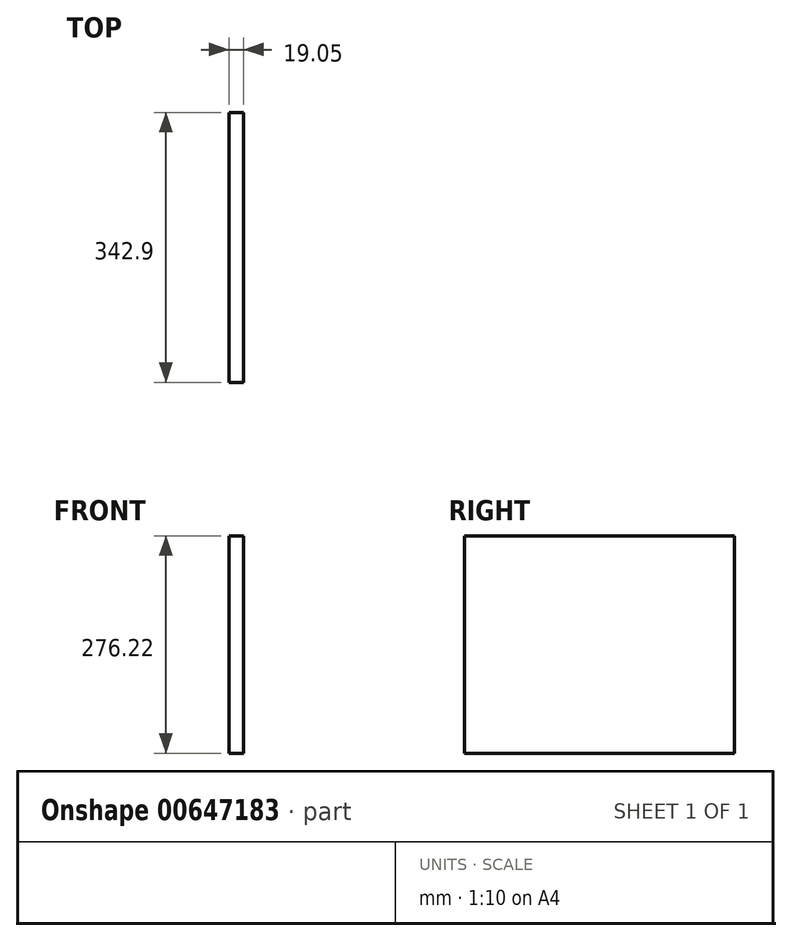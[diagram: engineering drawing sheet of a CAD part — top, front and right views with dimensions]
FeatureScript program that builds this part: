
annotation { "Feature Type Name" : "Feature", "Feature Type Description" : "" }
export const myFeature = defineFeature(function(context is Context, id is Id, definition is map)
    precondition{}
    {
        {
            var Q0;
            Q0=qCreatedBy(makeId("Right.planeOp"),FACE);
            var sketch = newSketch(context, id + "F0", { "sketchPlane" : qUnion([Q0])});
            skLineSegment(sketch, "E0.bottom", {"start": v(171.45, 138.11) * mm, "end": v(-171.45, 138.11) * mm});
            skLineSegment(sketch, "E0.top", {"start": v(171.45, -138.11) * mm, "end": v(-171.45, -138.11) * mm});
            skLineSegment(sketch, "E0.left", {"start": v(171.45, 138.11) * mm, "end": v(171.45, -138.11) * mm});
            skLineSegment(sketch, "E0.right", {"start": v(-171.45, 138.11) * mm, "end": v(-171.45, -138.11) * mm});
            skPoint(sketch, "E0.middle", {"position": v(0, 0) * mm});
            skSolve(sketch);
        }
        {
            var Q0;
            Q0=makeQuery(id+"F0.imprint","IMPRINT",FACE,{"disambiguationData":[TD([[makeQuery(id+"F0.imprint","IMPRINT",EDGE,{"derivedFrom":sQuery(id+"F0.wireOp",EDGE,"E0.bottom")}),1.0]])]});
            extrude(context, id + "F1", {"entities" : qUnion([Q0]), "depth" : 19.05 * mm, "offsetDistance" : 25.4 * mm});
        }
    });
